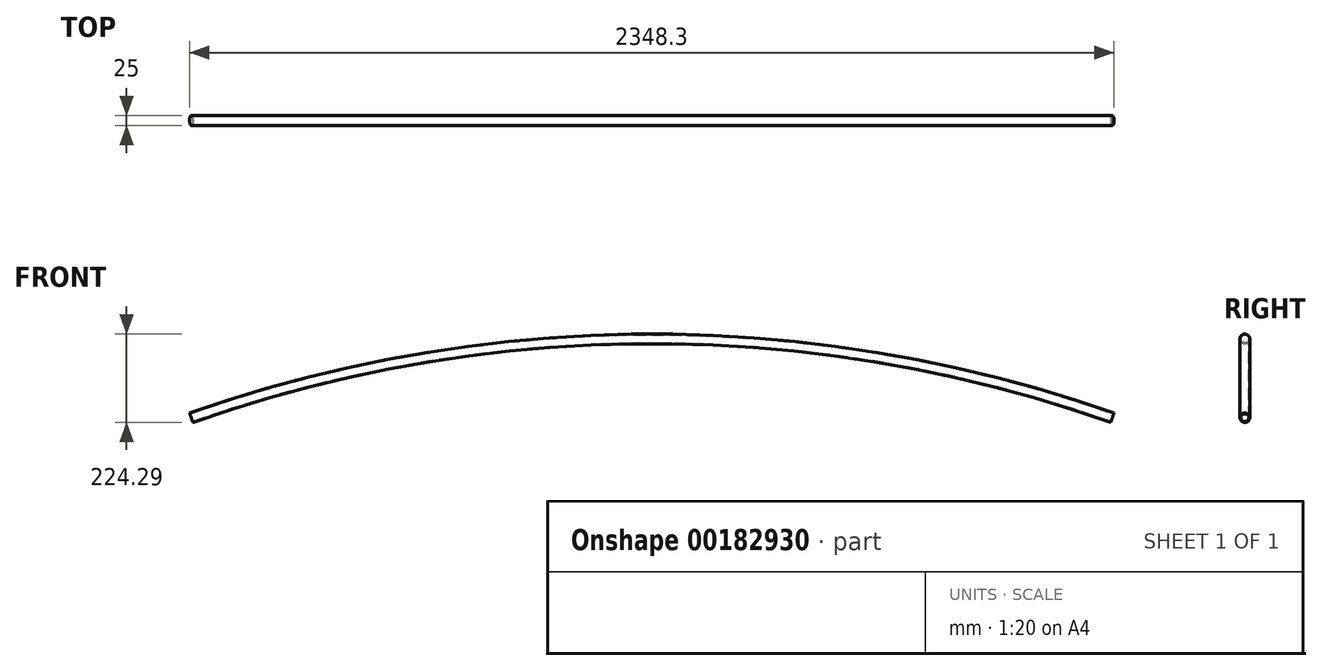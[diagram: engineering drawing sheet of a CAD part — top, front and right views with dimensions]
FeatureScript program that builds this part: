
annotation { "Feature Type Name" : "Feature", "Feature Type Description" : "" }
export const myFeature = defineFeature(function(context is Context, id is Id, definition is map)
    precondition{}
    {
        {
            var Q0;
            Q0=qCreatedBy(makeId("Front.planeOp"),FACE);
            var sketch = newSketch(context, id + "F0", { "sketchPlane" : qUnion([Q0])});
            skLineSegment(sketch, "E0", {"start": v(0, 0) * mm, "end": v(1170, 0) * mm});
            skLineSegment(sketch, "E1.MirrorCS", {"start": v(0, 0) * mm, "end": v(-1170, 0) * mm});
            skArc(sketch, "E2", {"start": v(1170, 0) * mm, "mid": v(0, 200) * mm, "end": v(-1170, 0) * mm});
            skLineSegment(sketch, "E3", {"start": v(0, 0) * mm, "end": v(0, 200) * mm});
            skSolve(sketch);
        }
        {
            var Q0;
            Q0=sQuery(id+"F0.wireOp",VERTEX,"E2.end");
            var Q1;
            Q1=sQuery(id+"F0.wireOp",EDGE,"E2");
            cPlane(context, id + "F1", {"entities" : qUnion([Q0, Q1]), "cplaneType" : CPlaneType.CURVE_POINT, "offset" : 25 * mm, "width" : 150 * mm, "height" : 150 * mm});
        }
        {
            var Q0;
            Q0=qCreatedBy(id+"F1.planeOp",FACE);
            var sketch = newSketch(context, id + "F2", { "sketchPlane" : qUnion([Q0])});
            skCircle(sketch, "E4", {"center": v(0, 388.64) * mm, "radius": 12.5 * mm});
            skCircle(sketch, "E5", {"center": v(0, 388.64) * mm, "radius": 10.5 * mm});
            skSolve(sketch);
        }
        {
            var Q0;
            Q0=makeQuery(id+"F2.imprint","IMPRINT",FACE,{"disambiguationData":[TD([[makeQuery(id+"F2.imprint","IMPRINT",EDGE,{"derivedFrom":sQuery(id+"F2.wireOp",EDGE,"E4")}),1.0]])]});
            var Q1;
            Q1=sQuery(id+"F0.wireOp",EDGE,"E2");
            sweep(context, id + "F3", {"profiles" : qUnion([Q0]), "path" : qUnion([Q1])});
        }
    });
